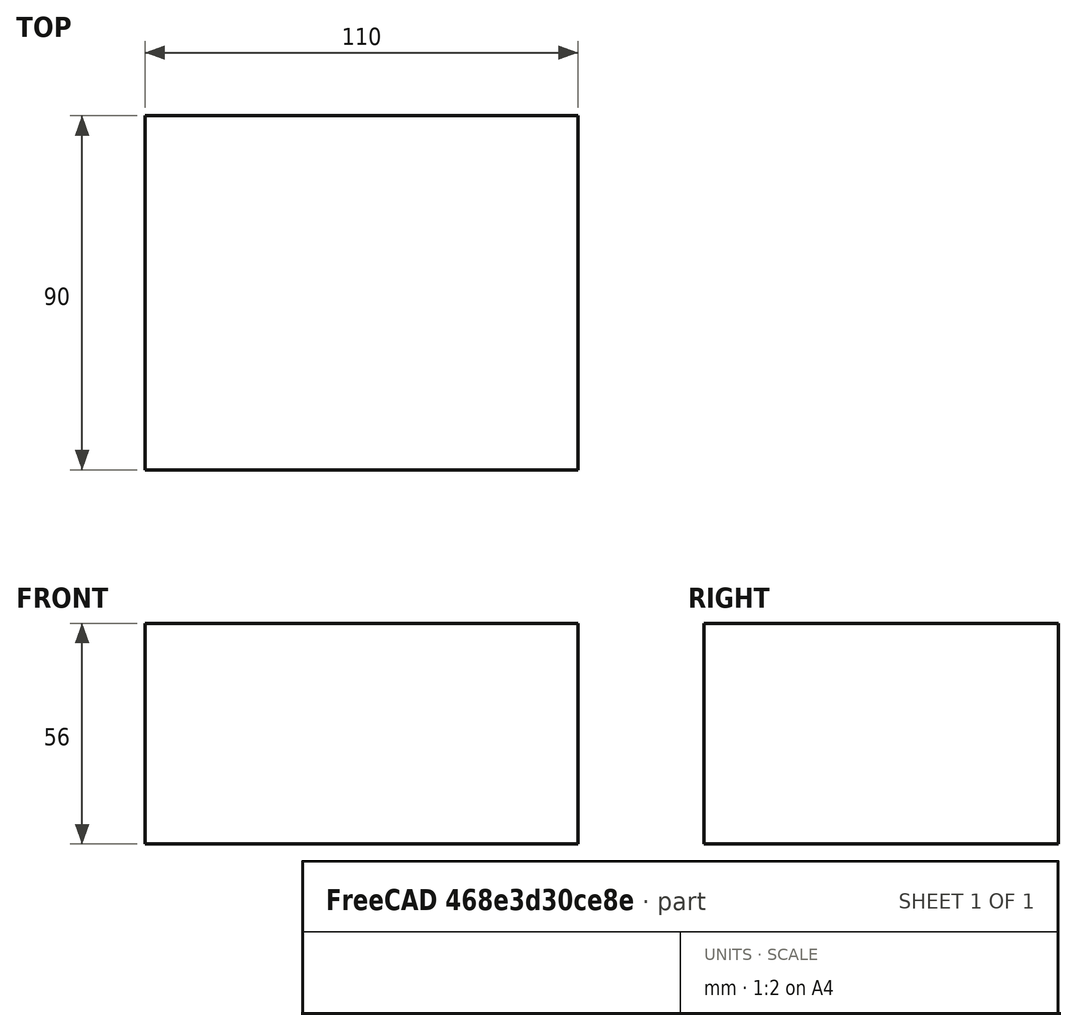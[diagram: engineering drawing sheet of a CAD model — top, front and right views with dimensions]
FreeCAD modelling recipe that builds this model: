
FCSTD DOCUMENT  (FreeCAD 0.19R)
Label: output
License: Creative Commons Attribution-ShareAlike
LicenseURL: http://creativecommons.org/licenses/by-sa/4.0/
objects: Path::FeaturePython×4, Part::FeaturePython×2, App::DocumentObjectGroup×2, App::Link×1, App::FeaturePython×1, Path::FeatureCompoundPython×1, Mesh::FeaturePython×1
note: 3 computed .brp shape members not serialized (recipe doc carries the construction recipe); baked Part::Feature solids carry a one-line shape summary decoded from their .brp
EXTERNAL_REF file=assembly.FCStd obj=Part

FEATURE [App::Link] Link  label="box"
  LinkedObject = -> <external assembly.FCStd>#Part
FEATURE [App::FeaturePython] SetupSheet  # Path/CAM operation (typed FeaturePython)
  ClearanceHeightExpression = OpStockZMax+SetupSheet.ClearanceHeightOffset
  ClearanceHeightOffset = 5
  CoolantMode = 0
  CoolantModes = None | Flood | Mist
  FinalDepthExpression = OpFinalDepth
  HorizRapid = 10
  SafeHeightExpression = OpStockZMax+SetupSheet.SafeHeightOffset
  SafeHeightOffset = 3
  StartDepthExpression = OpStartDepth
  StepDownExpression = OpToolDiameter
  VertRapid = 10
FEATURE [Part::FeaturePython] Clone  label="Model-box"  # Draft clone (typed FeaturePython)
  AttacherType = Attacher::AttachEngine3D
  Fuse = false
  Objects = -> [Link]
  PathResource = Model
  Placement = pos=(0,-3.6e-15,0) rot=(0,0,1;0rad)
  Scale = (1,1,1)
FEATURE [App::DocumentObjectGroup] Model
  Group = -> [Clone]
FEATURE [Path::FeaturePython] T1__Laser_0_2  label="T1: Laser 0.2"  # Path/CAM operation (typed FeaturePython)
  HorizFeed = 2
  HorizRapid = 10
  SpindleDir = 0
  SpindleSpeed = 70
  ToolNumber = 1
  VertFeed = 2
  VertRapid = 10
  expr: HorizRapid = SetupSheet.HorizRapid
  expr: VertRapid = SetupSheet.VertRapid
FEATURE [App::DocumentObjectGroup] Tools
  Group = -> [T1__Laser_0_2]
FEATURE [Path::FeaturePython] Profile  # Path/CAM operation (typed FeaturePython)
  Active = true
  AreaParams:
    Tolerance = 1e-07
    FitArcs = True
    Simplify = False
    CleanDistance = 0.0
    Accuracy = 0.01
    Unit = 1.0
    MinArcPoints = 4
    MaxArcPoints = 100
    ClipperScale = 10000000.0
    Fill = 0
    Coplanar = 0
    Reorient = True
    Outline = False
    Explode = False
    OpenMode = 0
    Deflection = 0.01
    SubjectFill = 0
    ClipFill = 0
    Offset = 0.1
    ExtraPass = 0
    Stepover = 0.0
    LastStepover = 0.0
    JoinType = 0
    EndType = 0
    MiterLimit = 2.0
    RoundPrecision = 0.0
    PocketMode = 0
    ToolRadius = 1.0
    PocketExtraOffset = 0.0
    PocketStepover = 0.0
    PocketLastStepover = 0.0
    FromCenter = False
    Angle = 45.0
    AngleShift = 0.0
    Shift = 0.0
    Thicken = False
    SectionCount = -1
    Stepdown = 1.0
    SectionOffset = 0.0
    SectionTolerance = 1e-06
    SectionMode = 2
    Project = False
  AttemptInverseAngle = true
  Base = -> [Clone]
  ClearanceHeight = 33
  CoolantMode = Mist
  CycleTime = 00:05:32
  Direction = 0
  EnableRotation = 0
  FinalDepth = 28
  HandleMultipleFeatures = 0
  InverseAngle = false
  JoinType = 0
  LimitDepthToFace = true
  MiterLimit = 0.1
  OffsetExtra = 0
  OpFinalDepth = 28
  OpStartDepth = 28.2
  OpStockZMax = 28
  OpStockZMin = -28
  OpToolDiameter = 0.2
  PathParams = {'orientation': 1, 'feedrate': 2.0, 'feedrate_v': 2.0, 'verbose': True, 'resume_height': 30.999999999999996, 'retraction': 33.0, 'return_end': True, 'preamble': False, 'start': Vector (-10.100000099999995, 4.8907878, 33.0)}
  ReverseDirection = false
  SafeHeight = 31
  Side = 0
  StartDepth = 28.2
  StartPoint = (0,0,0)
  StepDown = 0.2
  ToolController = -> T1__Laser_0_2
  UseComp = true
  UseStartPoint = false
  processCircles = true
  processHoles = true
  processPerimeter = true
  expr: ClearanceHeight = OpStockZMax + SetupSheet.ClearanceHeightOffset
  expr: SafeHeight = OpStockZMax + SetupSheet.SafeHeightOffset
  expr: StepDown = OpToolDiameter
  expr: FinalDepth = OpFinalDepth
  expr: StartDepth = OpStartDepth
FEATURE [Path::FeaturePython] DogboneDressup  # Path/CAM operation (typed FeaturePython)
  Base = -> Profile
  Custom = 0
  Incision = 0
  Side = 1
  Style = 0
FEATURE [Path::FeatureCompoundPython] Operations  # Path/CAM operation (typed FeaturePython)
  Group = -> [DogboneDressup]
  UsePlacements = false
FEATURE [Part::FeaturePython] Stock  # WARN: FeaturePython — macro-defined, semantics opaque (R4)
  Base = -> Model
  ExtXneg = 5
  ExtXpos = 5
  ExtYneg = 5
  ExtYpos = 5
  ExtZneg = 0
  ExtZpos = 0
  Placement = pos=(-50,-40,-28) rot=(0,0,1;0rad)
  StockType = FromBase
FEATURE [Path::FeaturePython] Job  # Path/CAM operation (typed FeaturePython)
  CycleTime = 00:05:32
  Fixtures = G54
  GeometryTolerance = 0.01
  Model = -> Model
  Operations = -> Operations
  OrderOutputBy = 0
  PostProcessor = 2
  PostProcessorOutputFile = <userpath>/mydata/github/FreeCAD/FreeCAD_lasercut_workflow/export/export_test_v1.dxf
  SetupSheet = -> SetupSheet
  SplitOutput = false
  Stock = -> Stock
  Tools = -> Tools
FEATURE [Mesh::FeaturePython] CutMaterial  # WARN: FeaturePython — macro-defined, semantics opaque (R4)
